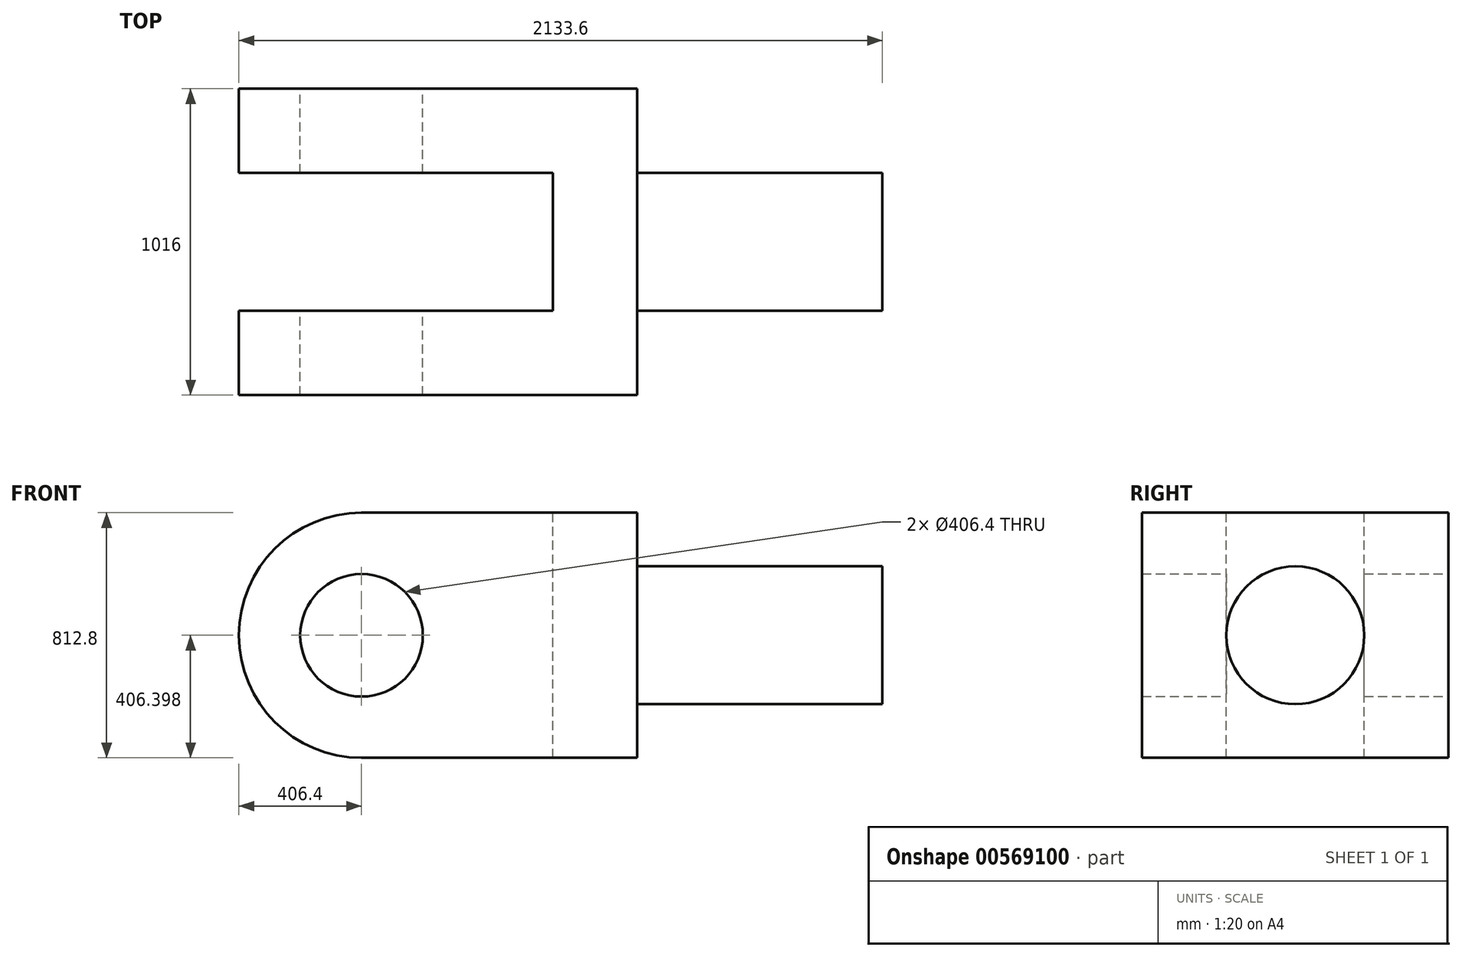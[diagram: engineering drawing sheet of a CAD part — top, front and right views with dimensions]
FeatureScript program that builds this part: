
annotation { "Feature Type Name" : "Feature", "Feature Type Description" : "" }
export const myFeature = defineFeature(function(context is Context, id is Id, definition is map)
    precondition{}
    {
        {
            var Q0;
            Q0=qCreatedBy(makeId("Front.planeOp"),FACE);
            var sketch = newSketch(context, id + "F0", { "sketchPlane" : qUnion([Q0])});
            skCircle(sketch, "E0", {"center": v(-334.24, 289.09) * mm, "radius": 203.2 * mm});
            skArc(sketch, "E1", {"start": v(-334.24, 695.49) * mm, "mid": v(-740.64, 289.09) * mm, "end": v(-334.24, -117.31) * mm});
            skLineSegment(sketch, "E2", {"start": v(-334.24, 695.49) * mm, "end": v(580.16, 695.49) * mm});
            skLineSegment(sketch, "E3", {"start": v(580.16, 695.49) * mm, "end": v(580.16, -117.31) * mm});
            skLineSegment(sketch, "E4", {"start": v(580.16, -117.31) * mm, "end": v(-334.24, -117.31) * mm});
            skSolve(sketch);
        }
        {
            var Q0;
            Q0=makeQuery(id+"F0.imprint","IMPRINT",FACE,{"disambiguationData":[TD([[makeQuery(id+"F0.imprint","IMPRINT",EDGE,{"derivedFrom":sQuery(id+"F0.wireOp",EDGE,"E0")}),-1.0]])]});
            extrude(context, id + "F1", {"entities" : qUnion([Q0]), "depth" : 1016 * mm, "offsetDistance" : 25.4 * mm});
        }
        {
            var Q0;
            Q0=makeQuery(id+"F1.opExtrude","SWEPT_FACE",FACE,{"disambiguationData":[OSD([sQuery(id+"F0.wireOp",EDGE,"E3")])]});
            var sketch = newSketch(context, id + "F2", { "sketchPlane" : qUnion([Q0])});
            skCircle(sketch, "E5", {"center": v(-508, 289.09) * mm, "radius": 228.6 * mm});
            skPoint(sketch, "E5.centerSnap0", {"position": v(-1016, 289.09) * mm});
            skPoint(sketch, "E5.centerSnap1", {"position": v(-508, 695.49) * mm});
            skSolve(sketch);
        }
        {
            var Q0;
            Q0=makeQuery(id+"F2.imprint","IMPRINT",FACE,{"disambiguationData":[TD([[makeQuery(id+"F2.imprint","IMPRINT",EDGE,{"derivedFrom":sQuery(id+"F2.wireOp",EDGE,"E5")}),1.0]])]});
            extrude(context, id + "F3", {"entities" : qUnion([Q0]), "operationType" : NewBodyOperationType.ADD, "depth" : 812.8 * mm, "offsetDistance" : 25.4 * mm});
        }
        {
            var Q0;
            Q0=makeQuery(id+"F1.opExtrude","SWEPT_FACE",FACE,{"disambiguationData":[OSD([sQuery(id+"F0.wireOp",EDGE,"E2")])]});
            var sketch = newSketch(context, id + "F4", { "sketchPlane" : qUnion([Q0])});
            skLineSegment(sketch, "E6", {"start": v(-334.24, -279.4) * mm, "end": v(300.76, -279.4) * mm});
            skLineSegment(sketch, "E7", {"start": v(300.76, -279.4) * mm, "end": v(300.76, -736.6) * mm});
            skLineSegment(sketch, "E8", {"start": v(300.76, -736.6) * mm, "end": v(-334.24, -736.6) * mm});
            skLineSegment(sketch, "E9", {"start": v(-334.24, -736.6) * mm, "end": v(-334.24, -279.4) * mm});
            skSolve(sketch);
        }
        {
            var Q0;
            Q0=makeQuery(id+"F4.imprint","IMPRINT",FACE,{"disambiguationData":[TD([[makeQuery(id+"F4.imprint","IMPRINT",EDGE,{"derivedFrom":sQuery(id+"F4.wireOp",EDGE,"E6")}),-1.0]])]});
            extrude(context, id + "F5", {"entities" : qUnion([Q0]), "operationType" : NewBodyOperationType.REMOVE, "endBound" : BoundingType.THROUGH_ALL, "oppositeDirection" : true, "depth" : 421.64 * mm, "offsetDistance" : 25.4 * mm});
        }
        {
            var Q0;
            Q0=makeQuery(id+"F5.boolean.opBoolean","COPY",FACE,{"disambiguationData":[TD([makeQuery(id+"F1.opExtrude","SWEPT_FACE",FACE,{"disambiguationData":[OSD([sQuery(id+"F0.wireOp",EDGE,"E2")])]})])],"derivedFrom":makeQuery(id+"F5.opExtrude","SWEPT_FACE",FACE,{"disambiguationData":[OSD([sQuery(id+"F4.wireOp",EDGE,"E9")])]})});
            extrude(context, id + "F6", {"entities" : qUnion([Q0]), "operationType" : NewBodyOperationType.REMOVE, "oppositeDirection" : true, "depth" : 568.96 * mm, "offsetDistance" : 25.4 * mm});
        }
        {
            var Q0;
            Q0=makeQuery(id+"F5.boolean.opBoolean","COPY",FACE,{"disambiguationData":[TD([makeQuery(id+"F1.opExtrude","SWEPT_FACE",FACE,{"disambiguationData":[OSD([sQuery(id+"F0.wireOp",EDGE,"E4")])]})])],"derivedFrom":makeQuery(id+"F5.opExtrude","SWEPT_FACE",FACE,{"disambiguationData":[OSD([sQuery(id+"F4.wireOp",EDGE,"E9")])]})});
            extrude(context, id + "F7", {"entities" : qUnion([Q0]), "operationType" : NewBodyOperationType.REMOVE, "oppositeDirection" : true, "depth" : 518.16 * mm, "offsetDistance" : 25.4 * mm});
        }
        {
            var Q0;
            Q0=makeQuery(id+"F7.boolean.opBoolean","COPY",FACE,{"derivedFrom":makeQuery(id+"F7.opExtrude","SWEPT_FACE",FACE,{"disambiguationData":[OSD([sQuery(id+"F0.wireOp",EDGE,"E0"),sQuery(id+"F4.wireOp",EDGE,"E9")])]})});
            extrude(context, id + "F8", {"entities" : qUnion([Q0]), "operationType" : NewBodyOperationType.REMOVE, "oppositeDirection" : true, "depth" : 731.52 * mm, "offsetDistance" : 25.4 * mm});
        }
        {
            var Q0;
            Q0=makeQuery(id+"F8.boolean.opBoolean","COPY",FACE,{"derivedFrom":makeQuery(id+"F8.opExtrude","SWEPT_FACE",FACE,{"disambiguationData":[OSD([sQuery(id+"F0.wireOp",EDGE,"E0"),sQuery(id+"F0.wireOp",EDGE,"E1"),sQuery(id+"F4.wireOp",EDGE,"E9")])]})});
            extrude(context, id + "F9", {"entities" : qUnion([Q0]), "operationType" : NewBodyOperationType.REMOVE, "oppositeDirection" : true, "depth" : 1033.78 * mm, "offsetDistance" : 25.4 * mm});
        }
    });
